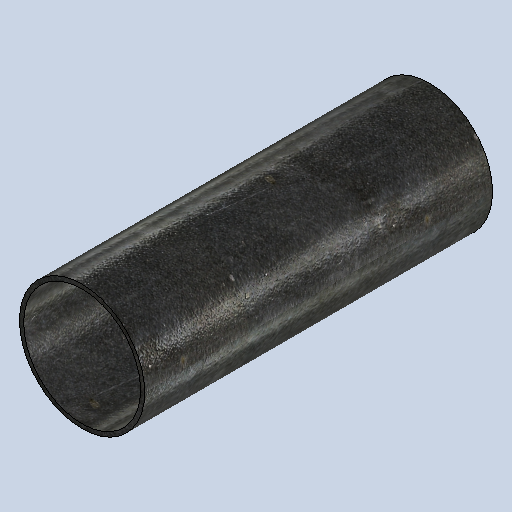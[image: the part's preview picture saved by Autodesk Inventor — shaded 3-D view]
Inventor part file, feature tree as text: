
AUTODESK INVENTOR PART (.ipt)
format: ipt  version: 2025.1 (Build 291241020, 241B)  size: 266,240 bytes
history: native  units: mm
features: extrude x1, sketch x1
ambient origin geometry x8: Origin, YZ Plane, XZ Plane, XY Plane, X Axis, Y Axis, Z Axis, Center Point
bodies: Solid1 (feature_tree)
feature tree (2):
  extrude  "Extrusion1"  Depth=250.0mm
  sketch  "Sketch1"  dims[d0=90.0mm d1=3.0mm d2=250.0mm d3=0.0mm]
